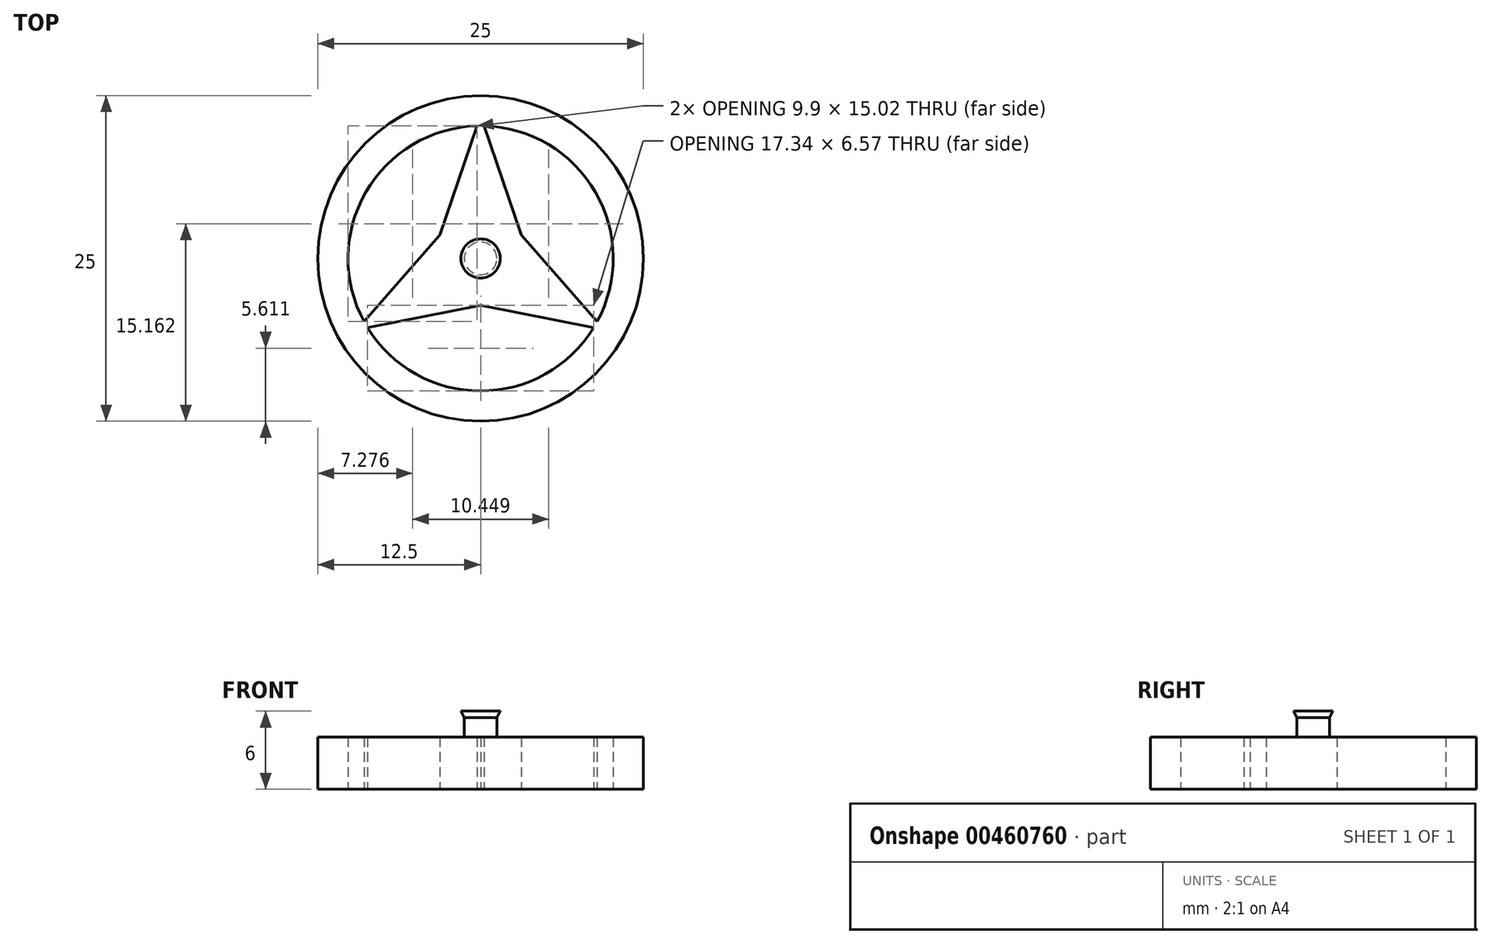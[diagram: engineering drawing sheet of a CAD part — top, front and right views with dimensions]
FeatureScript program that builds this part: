
annotation { "Feature Type Name" : "Feature", "Feature Type Description" : "" }
export const myFeature = defineFeature(function(context is Context, id is Id, definition is map)
    precondition{}
    {
        {
            var Q0;
            Q0=qCreatedBy(makeId("Top.planeOp"),FACE);
            var sketch = newSketch(context, id + "F0", { "sketchPlane" : qUnion([Q0])});
            skCircle(sketch, "E0", {"center": v(0, 0) * mm, "radius": 12.5 * mm});
            skLineSegment(sketch, "E1", {"start": v(0.27, 10.17) * mm, "end": v(3.12, 1.8) * mm});
            skLineSegment(sketch, "E2.MirrorCS", {"start": v(-0.27, 10.17) * mm, "end": v(-3.12, 1.8) * mm});
            skLineSegment(sketch, "E3.1.0", {"start": v(-8.67, -5.32) * mm, "end": v(0, -3.6) * mm});
            skLineSegment(sketch, "E3.1.3", {"start": v(-8.95, -4.85) * mm, "end": v(-3.12, 1.8) * mm});
            skLineSegment(sketch, "E3.2.0", {"start": v(8.95, -4.85) * mm, "end": v(3.12, 1.8) * mm});
            skLineSegment(sketch, "E3.2.3", {"start": v(8.67, -5.32) * mm, "end": v(0, -3.6) * mm});
            skArc(sketch, "E4", {"start": v(-0.27, 10.17) * mm, "mid": v(-8.81, 5.09) * mm, "end": v(-8.95, -4.85) * mm});
            skArc(sketch, "E5.trimOffspring", {"start": v(-8.67, -5.32) * mm, "mid": v(0, -10.18) * mm, "end": v(8.67, -5.32) * mm});
            skArc(sketch, "E6.trimOffspring", {"start": v(8.95, -4.85) * mm, "mid": v(8.81, 5.09) * mm, "end": v(0.27, 10.17) * mm});
            skSolve(sketch);
        }
        {
            var Q0;
            Q0 = qSketchRegion(id + "F0", true);
            extrude(context, id + "F1", {"entities" : qUnion([Q0]), "depth" : 4 * mm});
        }
        {
            var Q0;
            Q0=qCreatedBy(makeId("Front.planeOp"),FACE);
            var sketch = newSketch(context, id + "F2", { "sketchPlane" : qUnion([Q0])});
            skLineSegment(sketch, "E7", {"start": v(-1.25, 3.63) * mm, "end": v(-1.25, 5.5) * mm});
            skLineSegment(sketch, "E8", {"start": v(-1.25, 5.5) * mm, "end": v(-1.5, 6) * mm});
            skLineSegment(sketch, "E9", {"start": v(-1.5, 6) * mm, "end": v(0, 6) * mm});
            skLineSegment(sketch, "E10", {"start": v(0, 6) * mm, "end": v(0, 2.65) * mm});
            skLineSegment(sketch, "E11", {"start": v(0, 2.65) * mm, "end": v(-1.25, 3.63) * mm});
            skSolve(sketch);
        }
        {
            var Q0;
            Q0=makeQuery(id+"F2.imprint","IMPRINT",FACE,{"disambiguationData":[TD([[makeQuery(id+"F2.imprint","IMPRINT",EDGE,{"derivedFrom":sQuery(id+"F2.wireOp",EDGE,"E7")}),-1.0]])]});
            var Q1;
            Q1=sQuery(id+"F2.wireOp",EDGE,"E10");
            revolve(context, id + "F3", {"operationType" : NewBodyOperationType.ADD, "entities" : qUnion([Q0]), "axis" : qUnion([Q1]), "revolveType" : RevolveType.FULL});
        }
    });
